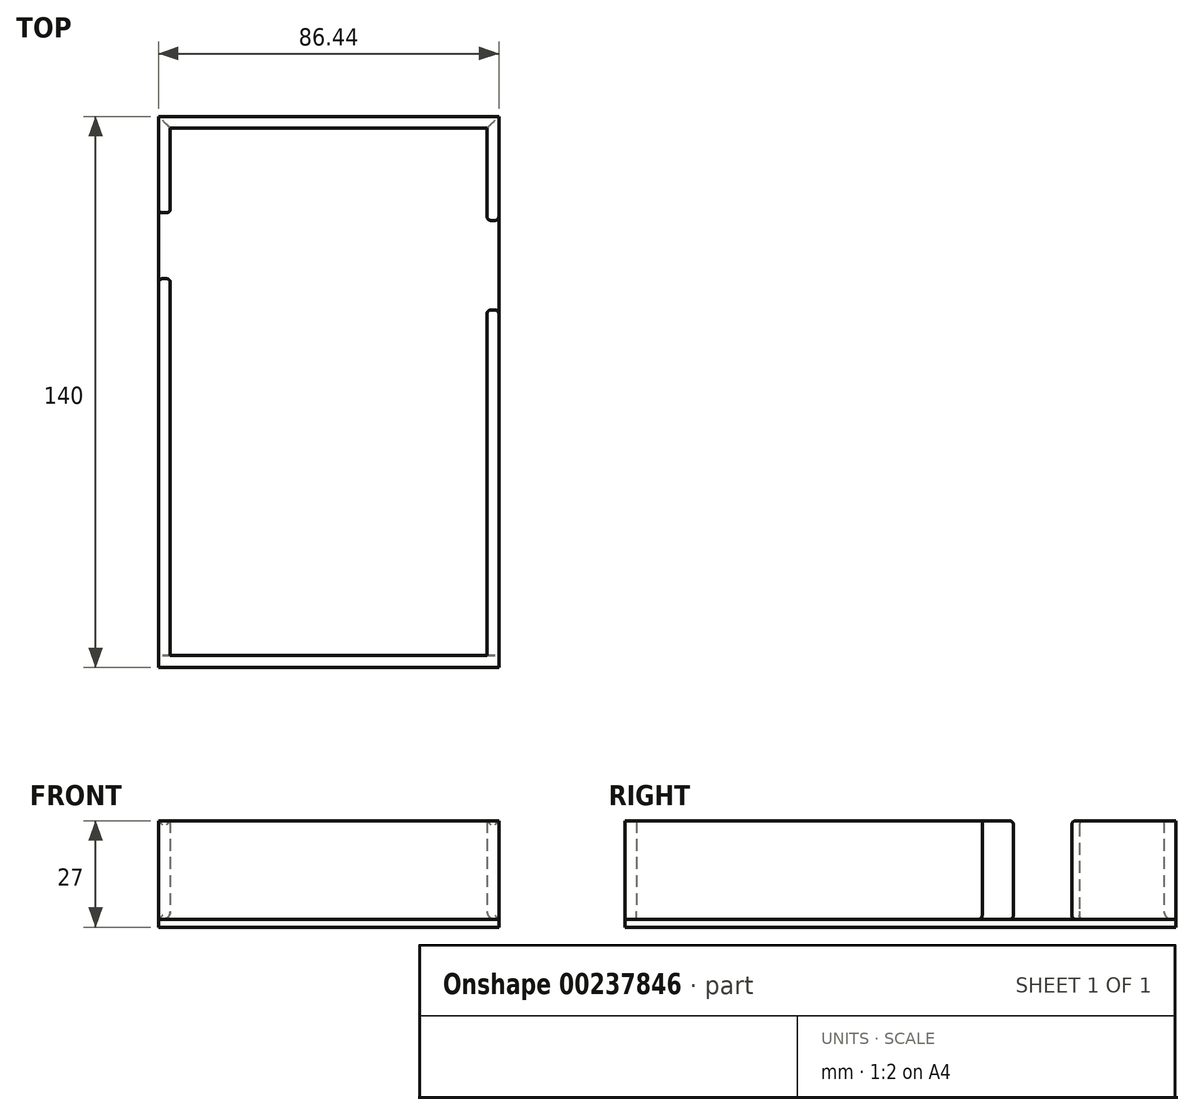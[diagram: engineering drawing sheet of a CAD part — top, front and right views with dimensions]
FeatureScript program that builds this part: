
annotation { "Feature Type Name" : "Feature", "Feature Type Description" : "" }
export const myFeature = defineFeature(function(context is Context, id is Id, definition is map)
    precondition{}
    {
        {
            var Q0;
            Q0=qCreatedBy(makeId("Top.planeOp"),FACE);
            var sketch = newSketch(context, id + "F0", { "sketchPlane" : qUnion([Q0])});
            skLineSegment(sketch, "E0.bottom", {"start": v(43.22, -70) * mm, "end": v(-43.22, -70) * mm});
            skLineSegment(sketch, "E0.top", {"start": v(43.22, 70) * mm, "end": v(-43.22, 70) * mm});
            skLineSegment(sketch, "E0.left", {"start": v(43.22, -70) * mm, "end": v(43.22, 70) * mm});
            skLineSegment(sketch, "E0.right", {"start": v(-43.22, -70) * mm, "end": v(-43.22, 70) * mm});
            skPoint(sketch, "E0.middle", {"position": v(0, 0) * mm});
            skSolve(sketch);
        }
        {
            var Q0;
            Q0=makeQuery(id+"F0.imprint","IMPRINT",FACE,{"disambiguationData":[TD([[makeQuery(id+"F0.imprint","IMPRINT",EDGE,{"derivedFrom":sQuery(id+"F0.wireOp",EDGE,"E0.bottom")}),-1.0]])]});
            extrude(context, id + "F1", {"entities" : qUnion([Q0]), "depth" : 2 * mm});
        }
        {
            var Q0;
            Q0=makeQuery(id+"F1.opExtrude","CAP_FACE",FACE,{"disambiguationData":[OSD([sQuery(id+"F0.wireOp",EDGE,"E0.bottom"),sQuery(id+"F0.wireOp",EDGE,"E0.top"),sQuery(id+"F0.wireOp",EDGE,"E0.left"),sQuery(id+"F0.wireOp",EDGE,"E0.right")])],"isStart":false});
            var sketch = newSketch(context, id + "F2", { "sketchPlane" : qUnion([Q0])});
            skLineSegment(sketch, "E1.bottom", {"start": v(43.22, -70) * mm, "end": v(-43.22, -70) * mm});
            skLineSegment(sketch, "E1.top", {"start": v(43.22, 70) * mm, "end": v(-43.22, 70) * mm});
            skLineSegment(sketch, "E1.left", {"start": v(43.22, -70) * mm, "end": v(43.22, 70) * mm});
            skLineSegment(sketch, "E1.right", {"start": v(-43.22, -70) * mm, "end": v(-43.22, 70) * mm});
            skPoint(sketch, "E1.middle", {"position": v(0, 0) * mm});
            skLineSegment(sketch, "E2.0", {"start": v(40.22, 67) * mm, "end": v(-40.22, 67) * mm});
            skLineSegment(sketch, "E2.1", {"start": v(40.22, -67) * mm, "end": v(40.22, 67) * mm});
            skLineSegment(sketch, "E2.2", {"start": v(40.22, -67) * mm, "end": v(-40.22, -67) * mm});
            skLineSegment(sketch, "E2.3", {"start": v(-40.22, -67) * mm, "end": v(-40.22, 67) * mm});
            skLineSegment(sketch, "E3.bottom", {"start": v(-43.22, 45.5) * mm, "end": v(-40.22, 45.5) * mm});
            skLineSegment(sketch, "E3.top", {"start": v(-43.22, 28.76) * mm, "end": v(-40.22, 28.76) * mm});
            skLineSegment(sketch, "E3.left", {"start": v(-43.22, 45.5) * mm, "end": v(-43.22, 28.76) * mm});
            skLineSegment(sketch, "E3.right", {"start": v(-40.22, 45.5) * mm, "end": v(-40.22, 28.76) * mm});
            skLineSegment(sketch, "E4.bottom", {"start": v(40.22, 43.56) * mm, "end": v(43.22, 43.56) * mm});
            skLineSegment(sketch, "E4.top", {"start": v(40.22, 20.8) * mm, "end": v(43.22, 20.8) * mm});
            skLineSegment(sketch, "E4.left", {"start": v(40.22, 43.56) * mm, "end": v(40.22, 20.8) * mm});
            skLineSegment(sketch, "E4.right", {"start": v(43.22, 43.56) * mm, "end": v(43.22, 20.8) * mm});
            skSolve(sketch);
        }
        {
            var Q0;
            {var subQ4=sQuery(id+"F2.wireOp",EDGE,"E1.bottom");Q0=makeQuery(id+"F2.imprint","IMPRINT",FACE,{"disambiguationData":[TD([[makeQuery(id+"F2.imprint","IMPRINT",EDGE,{"derivedFrom":subQ4}),-1.0]])]});}
            var Q1;
            {var subQ2=sQuery(id+"F2.wireOp",EDGE,"E1.top");Q1=makeQuery(id+"F2.imprint","IMPRINT",FACE,{"disambiguationData":[TD([[makeQuery(id+"F2.imprint","IMPRINT",EDGE,{"derivedFrom":subQ2}),1.0]])]});}
            extrude(context, id + "F3", {"entities" : qUnion([Q0, Q1]), "depth" : 25 * mm});
        }
        {
            var Q0;
            Q0=makeQuery(id+"F3.opExtrude","CAP_EDGE",EDGE,{"disambiguationData":[OSD([sQuery(id+"F2.wireOp",EDGE,"E2.0")])],"isStart":true});
            var Q1;
            {var subQ0=sQuery(id+"F2.wireOp",EDGE,"E2.1");Q1=makeQuery(id+"F3.opExtrude","CAP_EDGE",EDGE,{"disambiguationData":[OSD([subQ0]),TDD([makeQuery(id+"F2.imprint","IMPRINT",EDGE,{"disambiguationData":[TD([[makeQuery(id+"F2.imprint","INTERSECT",VERTEX,{"derivedFrom":[subQ0,sQuery(id+"F2.wireOp",EDGE,"E2.2")]}),-1.0]])],"derivedFrom":subQ0})])],"isStart":true});}
            var Q2;
            {var subQ0=sQuery(id+"F2.wireOp",EDGE,"E2.3");Q2=makeQuery(id+"F3.opExtrude","CAP_EDGE",EDGE,{"disambiguationData":[OSD([subQ0]),TDD([makeQuery(id+"F2.imprint","IMPRINT",EDGE,{"disambiguationData":[TD([[makeQuery(id+"F2.imprint","INTERSECT",VERTEX,{"derivedFrom":[sQuery(id+"F2.wireOp",EDGE,"E2.2"),subQ0]}),-1.0]])],"derivedFrom":subQ0})])],"isStart":true});}
            var Q3;
            {var subQ0=sQuery(id+"F2.wireOp",EDGE,"E2.3");Q3=makeQuery(id+"F3.opExtrude","CAP_EDGE",EDGE,{"disambiguationData":[OSD([subQ0]),TDD([makeQuery(id+"F2.imprint","IMPRINT",EDGE,{"disambiguationData":[TD([[makeQuery(id+"F2.imprint","INTERSECT",VERTEX,{"derivedFrom":[sQuery(id+"F2.wireOp",EDGE,"E2.0"),subQ0]}),1.0]])],"derivedFrom":subQ0})])],"isStart":true});}
            var Q4;
            {var subQ0=sQuery(id+"F2.wireOp",EDGE,"E2.1");Q4=makeQuery(id+"F3.opExtrude","CAP_EDGE",EDGE,{"disambiguationData":[OSD([subQ0]),TDD([makeQuery(id+"F2.imprint","IMPRINT",EDGE,{"disambiguationData":[TD([[makeQuery(id+"F2.imprint","INTERSECT",VERTEX,{"derivedFrom":[sQuery(id+"F2.wireOp",EDGE,"E2.0"),subQ0]}),1.0]])],"derivedFrom":subQ0})])],"isStart":true});}
            fillet(context, id + "F4", {"entities" : qUnion([Q0, Q1, Q2, Q3, Q4]), "radius" : 2 * mm, "tangentPropagation" : true, "allowEdgeOverflow" : false});
        }
        {
            var Q0;
            Q0=makeQuery(id+"F3.opExtrude","SWEPT_EDGE",EDGE,{"disambiguationData":[OSD([sQuery(id+"F2.wireOp",EDGE,"E2.3"),sQuery(id+"F2.wireOp",EDGE,"E3.top"),sQuery(id+"F2.wireOp",EDGE,"E3.right")])]});
            var Q1;
            Q1=makeQuery(id+"F3.opExtrude","SWEPT_EDGE",EDGE,{"disambiguationData":[OSD([sQuery(id+"F2.wireOp",EDGE,"E2.1"),sQuery(id+"F2.wireOp",EDGE,"E4.top"),sQuery(id+"F2.wireOp",EDGE,"E4.left")])]});
            var Q2;
            Q2=makeQuery(id+"F3.opExtrude","SWEPT_EDGE",EDGE,{"disambiguationData":[OSD([sQuery(id+"F2.wireOp",EDGE,"E1.left"),sQuery(id+"F2.wireOp",EDGE,"E4.top"),sQuery(id+"F2.wireOp",EDGE,"E4.right")])]});
            var Q3;
            Q3=makeQuery(id+"F3.opExtrude","SWEPT_FACE",FACE,{"disambiguationData":[OSD([sQuery(id+"F2.wireOp",EDGE,"E4.bottom")])]});
            var Q4;
            Q4=makeQuery(id+"F3.opExtrude","SWEPT_FACE",FACE,{"disambiguationData":[OSD([sQuery(id+"F2.wireOp",EDGE,"E3.bottom")])]});
            var Q5;
            Q5=makeQuery(id+"F3.opExtrude","SWEPT_FACE",FACE,{"disambiguationData":[OSD([sQuery(id+"F2.wireOp",EDGE,"E3.top")])]});
            var Q6;
            {var subQ0=sQuery(id+"F2.wireOp",EDGE,"E2.3");var subQ1=makeQuery(id+"F2.imprint","IMPRINT",EDGE,{"disambiguationData":[TD([[makeQuery(id+"F2.imprint","INTERSECT",VERTEX,{"derivedFrom":[sQuery(id+"F2.wireOp",EDGE,"E2.2"),subQ0]}),-1.0]])],"derivedFrom":subQ0});Q6=makeQuery(id+"F4.opFillet","BLEND_EDGE",EDGE,{"blendedFrom":[makeQuery(id+"F3.opExtrude","CAP_EDGE",EDGE,{"disambiguationData":[OSD([subQ0]),TDD([subQ1])],"isStart":true}),makeQuery(id+"F3.opExtrude","SWEPT_FACE",FACE,{"disambiguationData":[OSD([subQ0]),TDD([subQ1])]})],"blendedInto":[makeQuery(id+"F3.opExtrude","SWEPT_FACE",FACE,{"disambiguationData":[OSD([subQ0]),TDD([subQ1])]})]});}
            var Q7;
            {var subQ0=sQuery(id+"F2.wireOp",EDGE,"E2.1");var subQ1=makeQuery(id+"F2.imprint","IMPRINT",EDGE,{"disambiguationData":[TD([[makeQuery(id+"F2.imprint","INTERSECT",VERTEX,{"derivedFrom":[subQ0,sQuery(id+"F2.wireOp",EDGE,"E2.2")]}),-1.0]])],"derivedFrom":subQ0});Q7=makeQuery(id+"F4.opFillet","BLEND_EDGE",EDGE,{"blendedFrom":[makeQuery(id+"F3.opExtrude","CAP_EDGE",EDGE,{"disambiguationData":[OSD([subQ0]),TDD([subQ1])],"isStart":true}),makeQuery(id+"F3.opExtrude","SWEPT_FACE",FACE,{"disambiguationData":[OSD([subQ0]),TDD([subQ1])]})],"blendedInto":[makeQuery(id+"F3.opExtrude","SWEPT_FACE",FACE,{"disambiguationData":[OSD([subQ0]),TDD([subQ1])]})]});}
            fillet(context, id + "F5", {"entities" : qUnion([Q0, Q1, Q2, Q3, Q4, Q5, Q6, Q7]), "radius" : 1 * mm, "tangentPropagation" : true, "allowEdgeOverflow" : false});
        }
    });
